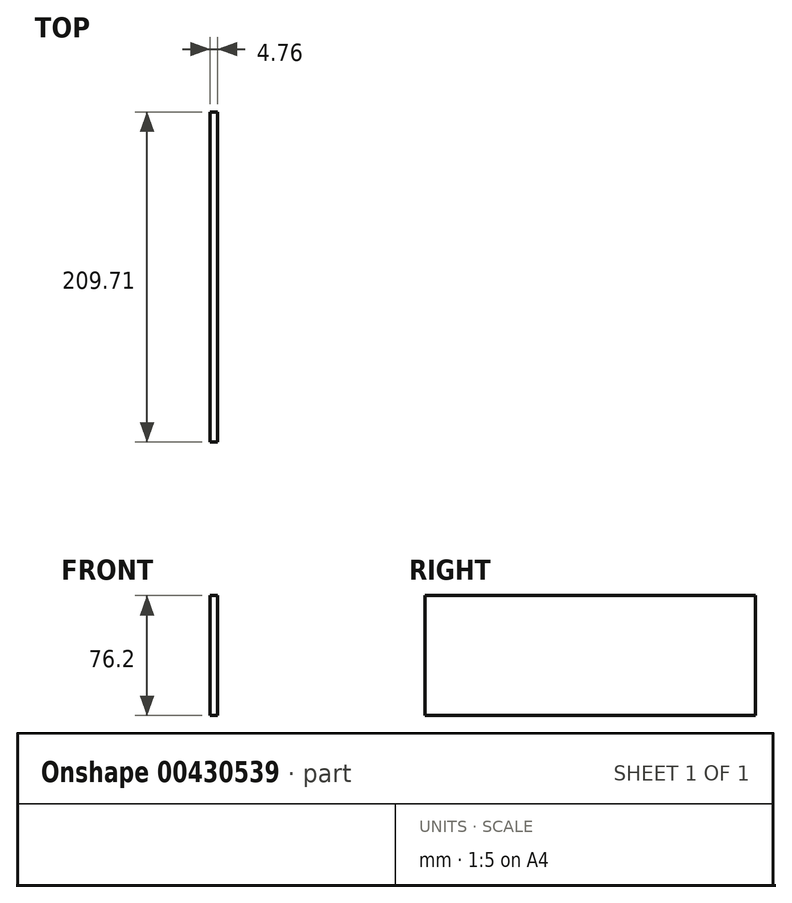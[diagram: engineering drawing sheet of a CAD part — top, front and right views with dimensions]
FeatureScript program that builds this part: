
annotation { "Feature Type Name" : "Feature", "Feature Type Description" : "" }
export const myFeature = defineFeature(function(context is Context, id is Id, definition is map)
    precondition{}
    {
        {
            var Q0;
            Q0=qCreatedBy(makeId("Right.planeOp"),FACE);
            var sketch = newSketch(context, id + "F0", { "sketchPlane" : qUnion([Q0])});
            skLineSegment(sketch, "E0.bottom", {"start": v(-117.88, -8.67) * mm, "end": v(91.83, -8.67) * mm});
            skLineSegment(sketch, "E0.top", {"start": v(-117.88, -84.87) * mm, "end": v(91.83, -84.87) * mm});
            skLineSegment(sketch, "E0.left", {"start": v(-117.88, -8.67) * mm, "end": v(-117.88, -84.87) * mm});
            skLineSegment(sketch, "E0.right", {"start": v(91.83, -8.67) * mm, "end": v(91.83, -84.87) * mm});
            skSolve(sketch);
        }
        {
            var Q0;
            Q0=makeQuery(id+"F0.imprint","IMPRINT",FACE,{"disambiguationData":[TD([[makeQuery(id+"F0.imprint","IMPRINT",EDGE,{"derivedFrom":sQuery(id+"F0.wireOp",EDGE,"E0.bottom")}),-1.0]])]});
            extrude(context, id + "F1", {"entities" : qUnion([Q0]), "depth" : 4.76 * mm});
        }
        {
            var Q0;
            Q0=makeQuery(id+"F0.imprint","IMPRINT",FACE,{"disambiguationData":[TD([[makeQuery(id+"F0.imprint","IMPRINT",EDGE,{"derivedFrom":sQuery(id+"F0.wireOp",EDGE,"E0.bottom")}),-1.0]])]});
            extrude(context, id + "F2", {"entities" : qUnion([Q0]), "depth" : 4.76 * mm});
        }
    });
